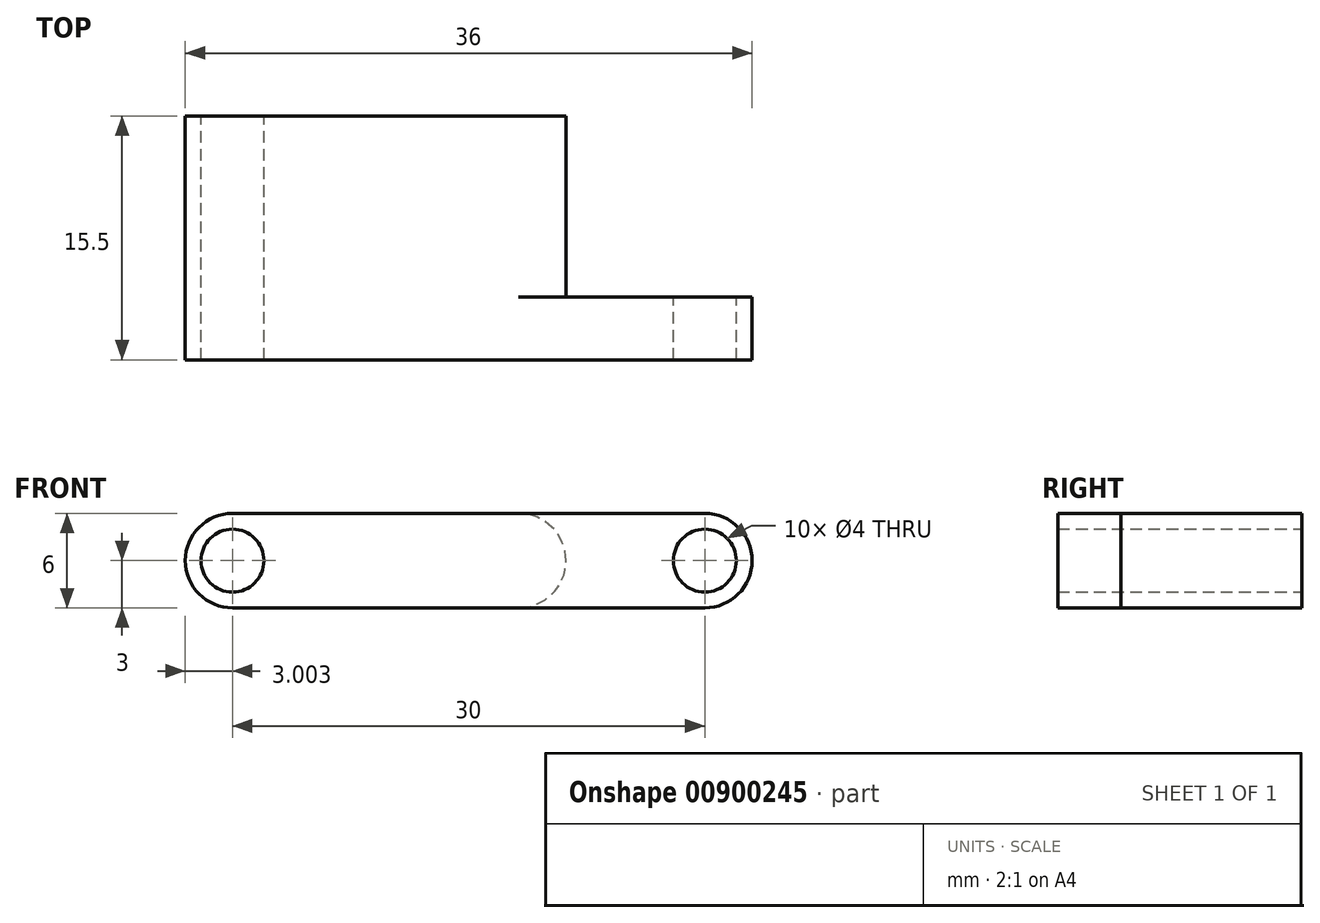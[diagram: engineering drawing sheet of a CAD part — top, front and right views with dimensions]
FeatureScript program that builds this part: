
annotation { "Feature Type Name" : "Feature", "Feature Type Description" : "" }
export const myFeature = defineFeature(function(context is Context, id is Id, definition is map)
    precondition{}
    {
        {
            var Q0;
            Q0=qCreatedBy(makeId("Front.planeOp"),FACE);
            var sketch = newSketch(context, id + "F0", { "sketchPlane" : qUnion([Q0])});
            skLineSegment(sketch, "E0", {"start": v(0, 4.92) * mm, "end": v(0, -5.72) * mm, "construction": true});
            skCircle(sketch, "E1", {"center": v(-18.18, 0) * mm, "radius": 2 * mm});
            skArc(sketch, "E2", {"start": v(-18.18, 3) * mm, "mid": v(-21.18, 0) * mm, "end": v(-18.18, -3) * mm});
            skCircle(sketch, "E3", {"center": v(0, 0) * mm, "radius": 3 * mm});
            skCircle(sketch, "E4", {"center": v(11.82, 0) * mm, "radius": 2 * mm});
            skArc(sketch, "E5", {"start": v(11.82, -3) * mm, "mid": v(14.82, 0) * mm, "end": v(11.82, 3) * mm});
            skLineSegment(sketch, "E6", {"start": v(-18.18, 3) * mm, "end": v(0, 3) * mm});
            skLineSegment(sketch, "E7", {"start": v(-18.18, -3) * mm, "end": v(0, -3) * mm});
            skLineSegment(sketch, "E8", {"start": v(0, 3) * mm, "end": v(11.82, 3) * mm});
            skLineSegment(sketch, "E9", {"start": v(0, -3) * mm, "end": v(11.82, -3) * mm});
            skLineSegment(sketch, "E10", {"start": v(-18.18, 3.99) * mm, "end": v(-18.18, -4.84) * mm, "construction": true});
            skSolve(sketch);
        }
        {
            var Q0;
            Q0=qSketchRegion(id+"F0",true);
            extrude(context, id + "F1", {"entities" : qUnion([Q0]), "depth" : 15.5 * mm, "offsetDistance" : 25 * mm});
        }
        {
            var Q0;
            Q0=makeQuery(id+"F0.imprint","IMPRINT",FACE,{"disambiguationData":[TD([[makeQuery(id+"F0.imprint","IMPRINT",EDGE,{"derivedFrom":sQuery(id+"F0.wireOp",EDGE,"E4")}),-1.0]])]});
            extrude(context, id + "F2", {"entities" : qUnion([Q0]), "operationType" : NewBodyOperationType.REMOVE, "depth" : (15.5 - 4) * mm, "offsetDistance" : 25 * mm});
        }
    });
